# Revit family: MO8X-DC02-6_RFA
name_source: partatom
category: Aparatos sanitarios
revit_build: Autodesk Revit 2016 (Build: 20150220_1215(x64)
units: mm (PartAtom-declared; Revit-internal decimal feet)

## family parameters
Compartido = No
Corte con vacíos al cargar = No
Cota de conector redondo = Diámetro de uso
Número OmniClass = 23.45.55.14
Punto de cálculo de habitación = No
Se basa en plano de trabajo = No
Siempre vertical = Sí
Tipo de pieza = Normal
Título OmniClass = Single Faucets

## types (1)
- MO8X-DC02-6
    Brass Chromed = Brass
    Comentarios de tipo = Single Control Faucet Lavatory
    Descripción = Deco Single Control Lavatory Without Drain
    Fabricante = HELVEX
    Features = Ceramic Cartridge
    Inlet Threads = ½" - 14 NPSM
    Max. Working Pressure = 85.3 psi
    Min. Working Pressure = 8.5 psi
    Modelo = MO8-DC-01
    Support Base Diameter = 2"
    Total Height = 9"
    Total Length = 7"

## geometry (parser evidence)
native form markers: Sweep x3
no freeform markers — native parametric forms only
